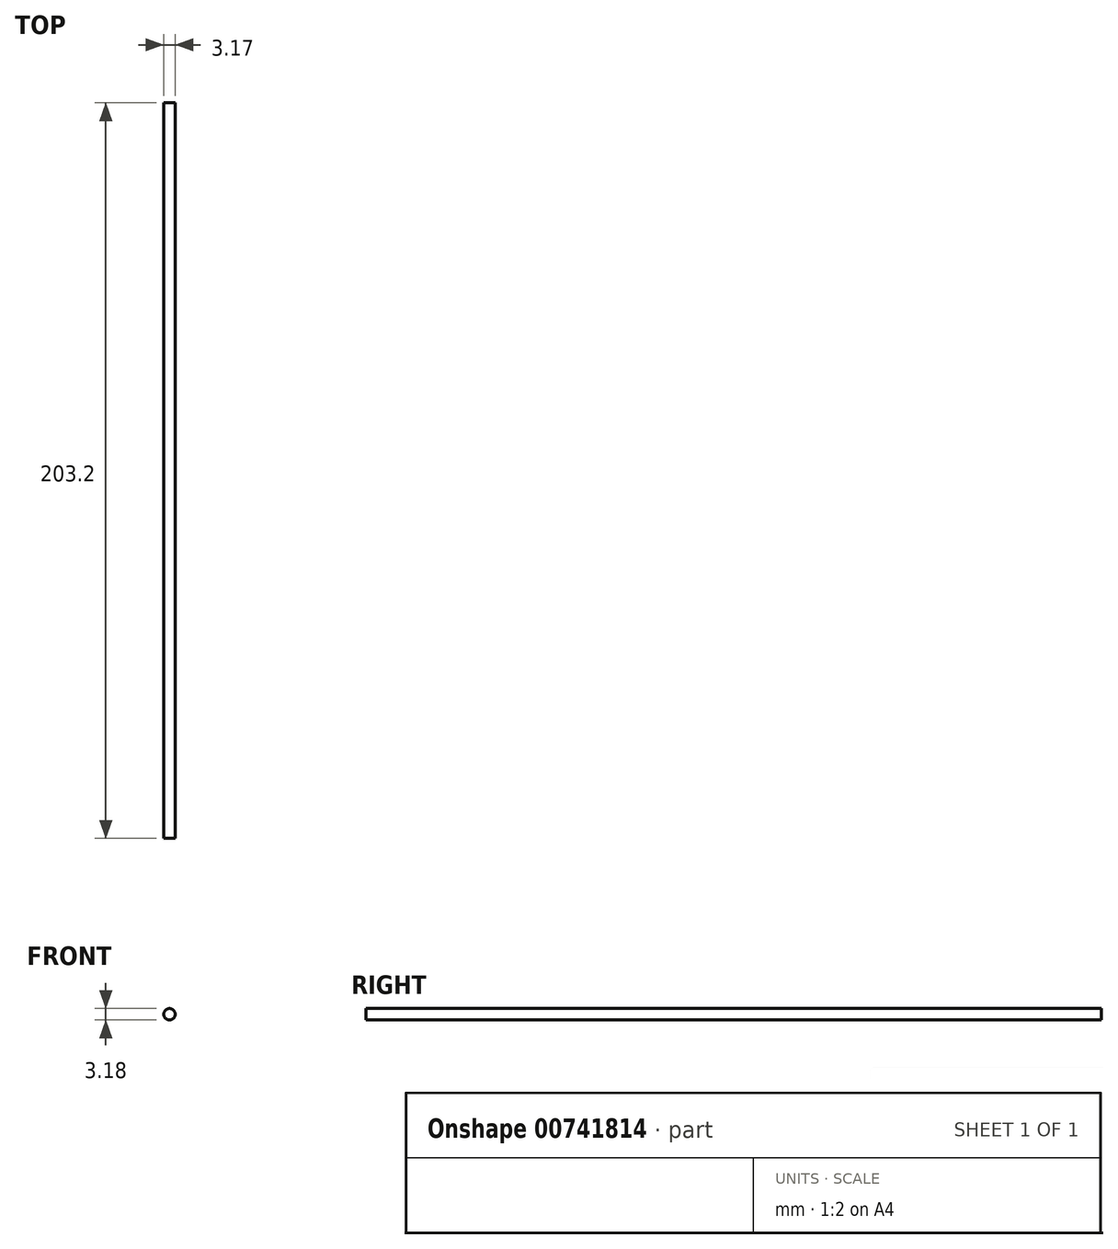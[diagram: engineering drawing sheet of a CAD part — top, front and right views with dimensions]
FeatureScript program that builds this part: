
annotation { "Feature Type Name" : "Feature", "Feature Type Description" : "" }
export const myFeature = defineFeature(function(context is Context, id is Id, definition is map)
    precondition{}
    {
        {
            var Q0;
            Q0=qCreatedBy(makeId("Front.planeOp"),FACE);
            var sketch = newSketch(context, id + "F0", { "sketchPlane" : qUnion([Q0])});
            skCircle(sketch, "E0", {"center": v(-28.42, 19.1) * mm, "radius": 1.59 * mm});
            skSolve(sketch);
        }
        {
            var Q0;
            Q0=makeQuery(id+"F0.imprint","IMPRINT",FACE,{"disambiguationData":[TD([[makeQuery(id+"F0.imprint","IMPRINT",EDGE,{"derivedFrom":sQuery(id+"F0.wireOp",EDGE,"E0")}),1.0]])]});
            extrude(context, id + "F1", {"entities" : qUnion([Q0]), "depth" : 203.2 * mm, "offsetDistance" : 25.4 * mm});
        }
    });
